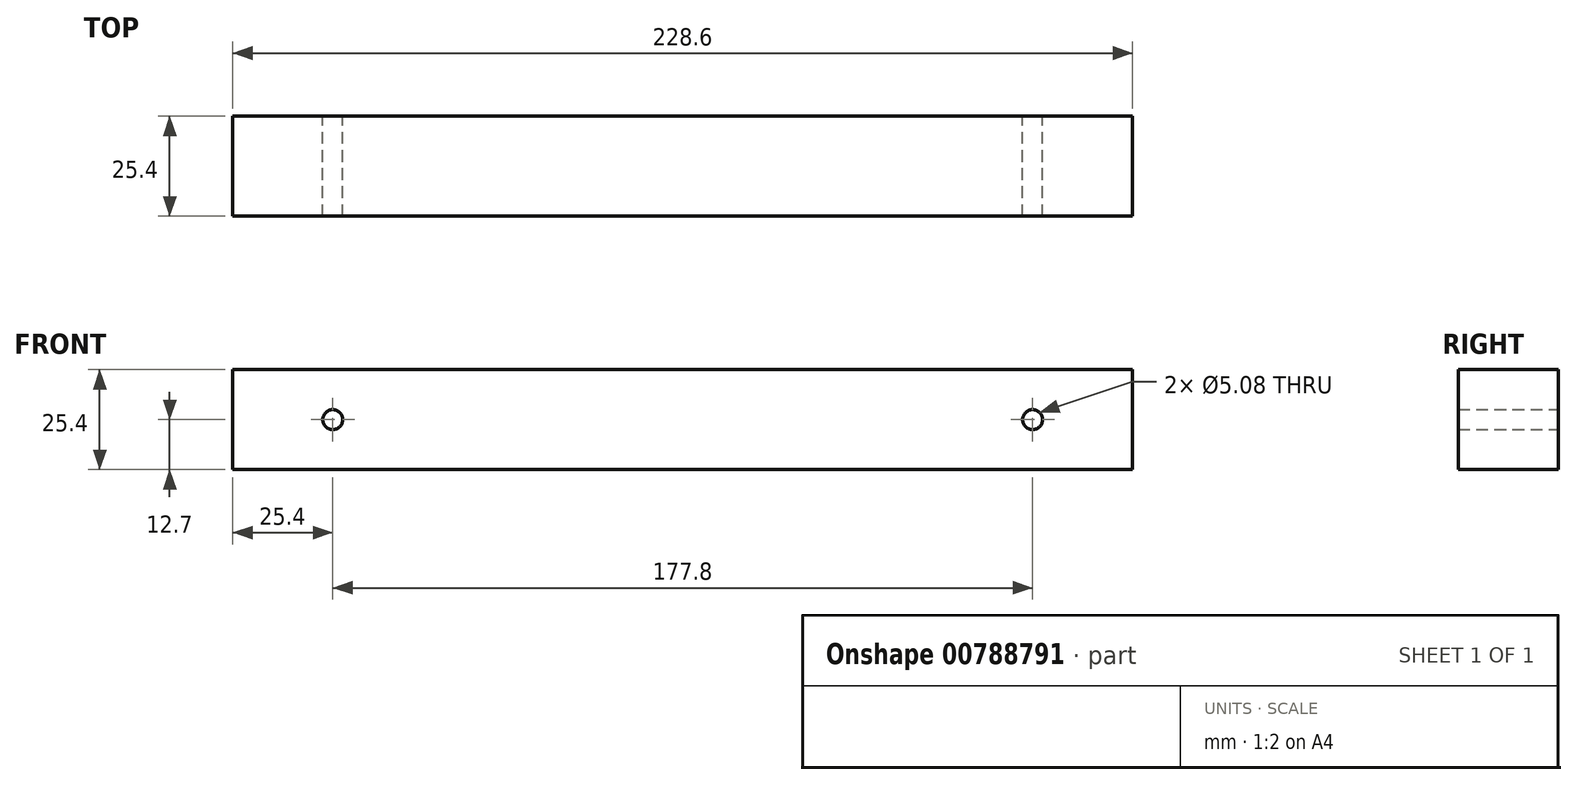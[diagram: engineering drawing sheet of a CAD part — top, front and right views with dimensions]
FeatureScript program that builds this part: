
annotation { "Feature Type Name" : "Feature", "Feature Type Description" : "" }
export const myFeature = defineFeature(function(context is Context, id is Id, definition is map)
    precondition{}
    {
        {
            var Q0;
            Q0=qCreatedBy(makeId("Front.planeOp"),FACE);
            var sketch = newSketch(context, id + "F0", { "sketchPlane" : qUnion([Q0])});
            skLineSegment(sketch, "E0.bottom", {"start": v(114.3, -12.7) * mm, "end": v(-114.3, -12.7) * mm});
            skLineSegment(sketch, "E0.top", {"start": v(114.3, 12.7) * mm, "end": v(-114.3, 12.7) * mm});
            skLineSegment(sketch, "E0.left", {"start": v(114.3, -12.7) * mm, "end": v(114.3, 12.7) * mm});
            skLineSegment(sketch, "E0.right", {"start": v(-114.3, -12.7) * mm, "end": v(-114.3, 12.7) * mm});
            skPoint(sketch, "E0.middle", {"position": v(0, 0) * mm});
            skCircle(sketch, "E1", {"center": v(-88.9, 0) * mm, "radius": 3.81 * mm});
            skCircle(sketch, "E2", {"center": v(88.9, 0) * mm, "radius": 2.54 * mm});
            skCircle(sketch, "E3", {"center": v(88.9, 0) * mm, "radius": 3.81 * mm});
            skCircle(sketch, "E4", {"center": v(-88.9, 0) * mm, "radius": 2.54 * mm});
            skSolve(sketch);
        }
        {
            var Q0;
            Q0=makeQuery(id+"F0.imprint","IMPRINT",FACE,{"disambiguationData":[TD([[makeQuery(id+"F0.imprint","IMPRINT",EDGE,{"derivedFrom":sQuery(id+"F0.wireOp",EDGE,"E0.bottom")}),-1.0]])]});
            var Q1;
            Q1=makeQuery(id+"F0.imprint","IMPRINT",FACE,{"disambiguationData":[TD([[makeQuery(id+"F0.imprint","IMPRINT",EDGE,{"derivedFrom":sQuery(id+"F0.wireOp",EDGE,"E2")}),-1.0]])]});
            var Q2;
            Q2=makeQuery(id+"F0.imprint","IMPRINT",FACE,{"disambiguationData":[TD([[makeQuery(id+"F0.imprint","IMPRINT",EDGE,{"derivedFrom":sQuery(id+"F0.wireOp",EDGE,"E1")}),1.0]])]});
            extrude(context, id + "F1", {"entities" : qUnion([Q0, Q1, Q2]), "depth" : 25.4 * mm, "offsetDistance" : 25.4 * mm, "symmetric" : true});
        }
    });
